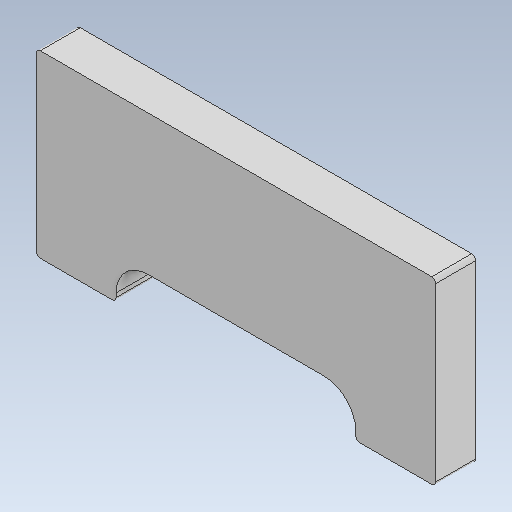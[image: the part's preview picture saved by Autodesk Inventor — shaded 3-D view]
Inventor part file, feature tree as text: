
AUTODESK INVENTOR PART (.ipt)
format: ipt  version: 2020 (Build 240168000, 168)  size: 109,056 bytes
history: native  units: mm
features: extrude x1, sketch x1
ambient origin geometry x8: Origin, YZ Plane, XZ Plane, XY Plane, X Axis, Y Axis, Z Axis, Center Point
bodies: Solid1 (feature_tree)
feature tree (2):
  extrude  "Extrusion1"  Depth=45.0mm
  sketch  "Sketch1"  dims[d0=100.0mm d1=45.0mm d2=20.0mm d3=10.0mm d4=8.0mm d5=1.0mm d6=1.0mm d7=10.0mm d8=0.0mm]
